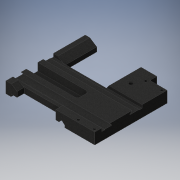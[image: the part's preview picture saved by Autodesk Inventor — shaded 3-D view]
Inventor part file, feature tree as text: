
AUTODESK INVENTOR PART (.ipt)
format: ipt  version: 2016 (Build 200138000, 138)  size: 293,376 bytes
history: native  units: in
note: dims shown in document units (in); Inventor stores cm internally (conversion verified against a paired STEP export)
features: extrude x13, sketch x10
ambient origin geometry x8: Origin, YZ Plane, XZ Plane, XY Plane, X Axis, Y Axis, Z Axis, Center Point
bodies: Solid1 (feature_tree)
feature tree (23):
  extrude  "Extrusion1"  Depth=13.5039in
  extrude  "Extrusion2"  Depth=1.9094in TaperAngle=0.0deg
  extrude  "Extrusion3"  Depth=1.378in
  extrude  "Extrusion4"  Depth=0.8933in
  extrude  "Extrusion8"  Depth=0.0787in
  extrude  "Extrusion19"  Depth=1.1811in
  extrude  "Extrusion20"  Depth=0.1181in
  extrude  "Extrusion21"  Depth=0.3937in
  extrude  "Extrusion22"  Depth=1.2992in
  extrude  "Extrusion23"  Depth=5.5118in
  extrude  "Extrusion24"  Depth=5.5118in
  extrude  "Extrusion25"  TaperAngle=0.0deg  [1 undecoded]
  extrude  "Extrusion26"  Depth=0.0787in TaperAngle=0.0deg
  sketch  "Sketch1"  dims[d0=15.1181in d1=13.5039in]
  sketch  "Sketch12"  dims[d2=1.9094in d3=0.0in d12=1.9094in d13=0.0in]
  sketch  "Sketch28"  dims[d23=1.378in d27=3.7795in]
  sketch  "Sketch29"  dims[d29=1.7323in d32=0.8933in]
  sketch  "Sketch30"  dims[d35=1.9094in d36=0.0in d37=0.0787in]
  sketch  "Sketch32"  dims[d38=0.5118in d43=1.1811in]
  sketch  "Sketch36"  dims[d44=1.9094in d45=0.0in d46=0.1181in]
  sketch  "Sketch37"  dims[d52=0.3436in d72=0.3937in]
  sketch  "Sketch38"  dims[d73=1.2992in d74=0.0in d146=0.4567in]
  sketch  "Sketch40"  dims[d149=0.4567in d152=0.4567in d155=0.4567in d156=0.0in d157=0.0in d159=0.0787in d160=0.0in d161=0.0787in d162=0.0in d168=0.6299in d169=0.3937in d170=0.0in d209=0.6299in d210=45.0deg d211=0.1811in d214=0.5197in d215=45.0deg d216=0.4724in d224=0.8661in d225=0.3937in d227=0.3937in d228=0.0in d229=0.5512in d232=0.748in d233=5.5118in d234=0.0in d235=5.5118in d236=0.0in d240=0.5197in d242=0.1811in d243=0.6299in d245=5.5118in d246=0.0in]
note: 1 required parameter value undecoded (feature->parameter linkage not recoverable at this tier; creation-order binding heuristic only, values carry confidence <= 0.55)
